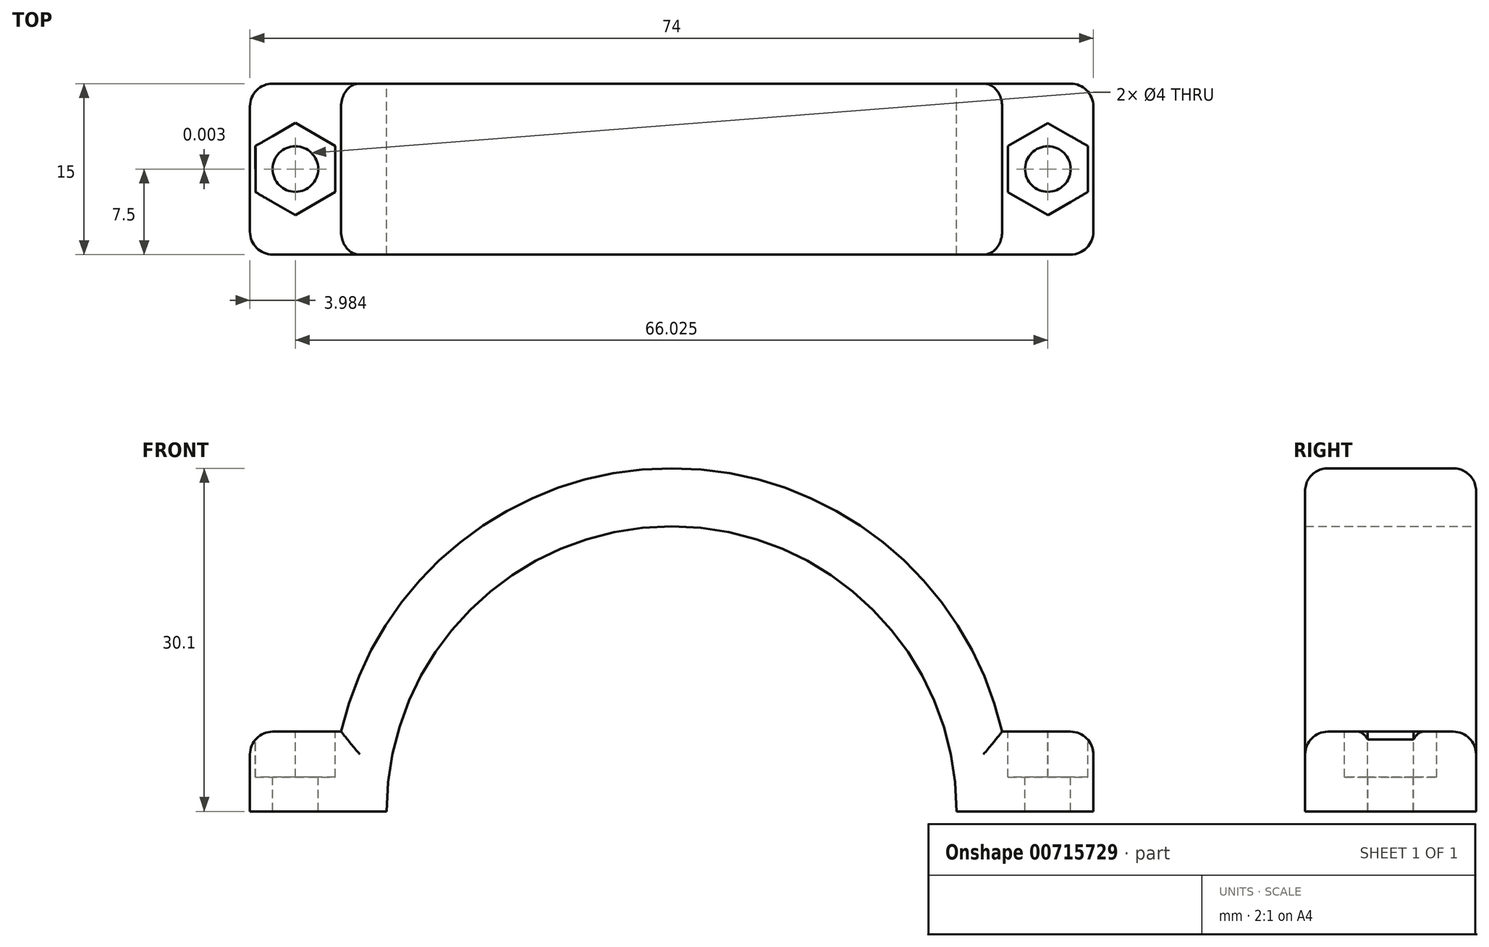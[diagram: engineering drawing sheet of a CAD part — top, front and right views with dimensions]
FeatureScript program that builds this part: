
annotation { "Feature Type Name" : "Feature", "Feature Type Description" : "" }
export const myFeature = defineFeature(function(context is Context, id is Id, definition is map)
    precondition{}
    {
        {
            var Q0;
            Q0=qCreatedBy(makeId("Front.planeOp"),FACE);
            var sketch = newSketch(context, id + "F0", { "sketchPlane" : qUnion([Q0])});
            skArc(sketch, "E0", {"start": v(26.87, 0.03) * mm, "mid": v(1.87, 25.02) * mm, "end": v(-23.13, 0.03) * mm});
            skLineSegment(sketch, "E1", {"start": v(26.87, 0.03) * mm, "end": v(38.87, 0.03) * mm});
            skLineSegment(sketch, "E2", {"start": v(38.87, 0.03) * mm, "end": v(38.87, 7.03) * mm});
            skLineSegment(sketch, "E3", {"start": v(38.87, 7.03) * mm, "end": v(30.87, 7.03) * mm});
            skLineSegment(sketch, "E4", {"start": v(-23.13, 0.03) * mm, "end": v(-35.13, 0.03) * mm});
            skLineSegment(sketch, "E5", {"start": v(-35.13, 0.03) * mm, "end": v(-35.13, 7.03) * mm});
            skLineSegment(sketch, "E6", {"start": v(-35.13, 7.03) * mm, "end": v(-27.13, 7.03) * mm});
            skArc(sketch, "E7", {"start": v(30.87, 7.03) * mm, "mid": v(1.87, 30.13) * mm, "end": v(-27.13, 7.03) * mm});
            skSolve(sketch);
        }
        {
            var Q0;
            Q0 = qSketchRegion(id + "F0", true);
            extrude(context, id + "F1", {"entities" : qUnion([Q0]), "depth" : 15 * mm, "offsetDistance" : 25 * mm});
        }
        {
            var Q0;
            Q0=makeQuery(id+"F1.opExtrude","CAP_EDGE",EDGE,{"disambiguationData":[OSD([sQuery(id+"F0.wireOp",EDGE,"E7")])],"isStart":false});
            var Q1;
            Q1=makeQuery(id+"F1.opExtrude","CAP_EDGE",EDGE,{"disambiguationData":[OSD([sQuery(id+"F0.wireOp",EDGE,"E3")])],"isStart":false});
            var Q2;
            Q2=makeQuery(id+"F1.opExtrude","CAP_EDGE",EDGE,{"disambiguationData":[OSD([sQuery(id+"F0.wireOp",EDGE,"E2")])],"isStart":false});
            var Q3;
            Q3=makeQuery(id+"F1.opExtrude","SWEPT_EDGE",EDGE,{"disambiguationData":[OSD([sQuery(id+"F0.wireOp",EDGE,"E2"),sQuery(id+"F0.wireOp",EDGE,"E3")])]});
            var Q4;
            Q4=makeQuery(id+"F1.opExtrude","CAP_EDGE",EDGE,{"disambiguationData":[OSD([sQuery(id+"F0.wireOp",EDGE,"E6")])],"isStart":false});
            var Q5;
            Q5=makeQuery(id+"F1.opExtrude","CAP_EDGE",EDGE,{"disambiguationData":[OSD([sQuery(id+"F0.wireOp",EDGE,"E5")])],"isStart":false});
            var Q6;
            Q6=makeQuery(id+"F1.opExtrude","SWEPT_EDGE",EDGE,{"disambiguationData":[OSD([sQuery(id+"F0.wireOp",EDGE,"E5"),sQuery(id+"F0.wireOp",EDGE,"E6")])]});
            var Q7;
            Q7=makeQuery(id+"F1.opExtrude","CAP_EDGE",EDGE,{"disambiguationData":[OSD([sQuery(id+"F0.wireOp",EDGE,"E7")])],"isStart":true});
            var Q8;
            Q8=makeQuery(id+"F1.opExtrude","CAP_EDGE",EDGE,{"disambiguationData":[OSD([sQuery(id+"F0.wireOp",EDGE,"E6")])],"isStart":true});
            var Q9;
            Q9=makeQuery(id+"F1.opExtrude","CAP_EDGE",EDGE,{"disambiguationData":[OSD([sQuery(id+"F0.wireOp",EDGE,"E5")])],"isStart":true});
            var Q10;
            Q10=makeQuery(id+"F1.opExtrude","CAP_EDGE",EDGE,{"disambiguationData":[OSD([sQuery(id+"F0.wireOp",EDGE,"E3")])],"isStart":true});
            var Q11;
            Q11=makeQuery(id+"F1.opExtrude","CAP_EDGE",EDGE,{"disambiguationData":[OSD([sQuery(id+"F0.wireOp",EDGE,"E2")])],"isStart":true});
            fillet(context, id + "F2", {"entities" : qUnion([Q0, Q1, Q2, Q3, Q4, Q5, Q6, Q7, Q8, Q9, Q10, Q11]), "radius" : 2 * mm, "tangentPropagation" : true, "allowEdgeOverflow" : false});
        }
        {
            var Q0;
            Q0=makeQuery(id+"F1.opExtrude","SWEPT_FACE",FACE,{"disambiguationData":[OSD([sQuery(id+"F0.wireOp",EDGE,"E3")])]});
            var sketch = newSketch(context, id + "F3", { "sketchPlane" : qUnion([Q0])});
            skCircle(sketch, "E8", {"center": v(34.88, -7.5) * mm, "radius": 2 * mm});
            skCircle(sketch, "E9.cCircle", {"center": v(34.88, -7.5) * mm, "radius": 3.5 * mm, "construction": true});
            skLineSegment(sketch, "E9.0", {"start": v(31.38, -5.49) * mm, "end": v(34.87, -3.46) * mm});
            skLineSegment(sketch, "E9.1", {"start": v(34.87, -3.46) * mm, "end": v(38.38, -5.47) * mm});
            skLineSegment(sketch, "E9.2", {"start": v(38.38, -5.47) * mm, "end": v(38.38, -9.51) * mm});
            skLineSegment(sketch, "E9.3", {"start": v(38.38, -9.51) * mm, "end": v(34.89, -11.54) * mm});
            skLineSegment(sketch, "E9.4", {"start": v(34.89, -11.54) * mm, "end": v(31.38, -9.53) * mm});
            skLineSegment(sketch, "E9.5", {"start": v(31.38, -9.53) * mm, "end": v(31.38, -5.49) * mm});
            skPoint(sketch, "E9.0.midPoint", {"position": v(33.12, -4.47) * mm});
            skSolve(sketch);
        }
        {
            var Q0;
            {var subQ0=sQuery(id+"F3.wireOp",EDGE,"E8");var subQ1=sQuery(id+"F0.wireOp",EDGE,"E3");var subQ2=makeQuery(id+"F2.opFillet","BLEND_EDGE",EDGE,{"blendedFrom":[makeQuery(id+"F1.opExtrude","SWEPT_EDGE",EDGE,{"disambiguationData":[OSD([sQuery(id+"F0.wireOp",EDGE,"E2"),subQ1])]}),makeQuery(id+"F1.opExtrude","SWEPT_FACE",FACE,{"disambiguationData":[OSD([subQ1])]})],"blendedInto":[makeQuery(id+"F1.opExtrude","SWEPT_FACE",FACE,{"disambiguationData":[OSD([subQ1])]})]});var subQ3=makeQuery(id+"F3.imprint","INTERSECT",VERTEX,{"disambiguationData":[OD(0.0)],"derivedFrom":[subQ2,subQ0]});Q0=makeQuery(id+"F3.imprint","IMPRINT",FACE,{"disambiguationData":[TD([[makeQuery(id+"F3.imprint","IMPRINT",EDGE,{"disambiguationData":[TD([[subQ3,-1.0]])],"derivedFrom":subQ0}),1.0]])]});}
            extrude(context, id + "F4", {"entities" : qUnion([Q0]), "operationType" : NewBodyOperationType.REMOVE, "oppositeDirection" : true, "depth" : 25 * mm, "offsetDistance" : 25 * mm});
        }
        {
            var Q0;
            {var subQ1=sQuery(id+"F3.wireOp",EDGE,"E9.0");Q0=makeQuery(id+"F3.imprint","IMPRINT",FACE,{"disambiguationData":[TD([[makeQuery(id+"F3.imprint","IMPRINT",EDGE,{"derivedFrom":subQ1}),-1.0]])]});}
            var Q1;
            {var subQ0=sQuery(id+"F3.wireOp",EDGE,"E9.2");Q1=makeQuery(id+"F3.imprint","IMPRINT",FACE,{"disambiguationData":[TD([[makeQuery(id+"F3.imprint","IMPRINT",EDGE,{"derivedFrom":subQ0}),-1.0]])]});}
            extrude(context, id + "F5", {"entities" : qUnion([Q0, Q1]), "operationType" : NewBodyOperationType.REMOVE, "oppositeDirection" : true, "depth" : 4 * mm, "offsetDistance" : 25 * mm});
        }
        {
            var Q0;
            {var subQ0=sQuery(id+"F3.wireOp",EDGE,"E8");var subQ1=sQuery(id+"F0.wireOp",EDGE,"E3");var subQ2=makeQuery(id+"F2.opFillet","BLEND_EDGE",EDGE,{"blendedFrom":[makeQuery(id+"F1.opExtrude","SWEPT_EDGE",EDGE,{"disambiguationData":[OSD([sQuery(id+"F0.wireOp",EDGE,"E2"),subQ1])]}),makeQuery(id+"F1.opExtrude","SWEPT_FACE",FACE,{"disambiguationData":[OSD([subQ1])]})],"blendedInto":[makeQuery(id+"F1.opExtrude","SWEPT_FACE",FACE,{"disambiguationData":[OSD([subQ1])]})]});var subQ3=makeQuery(id+"F3.imprint","INTERSECT",VERTEX,{"disambiguationData":[OD(0.0)],"derivedFrom":[subQ2,subQ0]});Q0=makeQuery(id+"F3.imprint","IMPRINT",FACE,{"disambiguationData":[TD([[makeQuery(id+"F3.imprint","IMPRINT",EDGE,{"disambiguationData":[TD([[subQ3,1.0]])],"derivedFrom":subQ0}),1.0]])]});}
            extrude(context, id + "F6", {"entities" : qUnion([Q0]), "operationType" : NewBodyOperationType.REMOVE, "oppositeDirection" : true, "depth" : 25 * mm, "offsetDistance" : 25 * mm});
        }
        {
            var Q0;
            Q0=makeQuery(id+"F1.opExtrude","SWEPT_FACE",FACE,{"disambiguationData":[OSD([sQuery(id+"F0.wireOp",EDGE,"E6")])]});
            var sketch = newSketch(context, id + "F7", { "sketchPlane" : qUnion([Q0])});
            skCircle(sketch, "E10", {"center": v(-31.15, -7.5) * mm, "radius": 2 * mm});
            skCircle(sketch, "E11.cCircle", {"center": v(-31.15, -7.5) * mm, "radius": 3.5 * mm, "construction": true});
            skLineSegment(sketch, "E11.0", {"start": v(-34.65, -5.48) * mm, "end": v(-31.15, -3.46) * mm});
            skLineSegment(sketch, "E11.1", {"start": v(-31.15, -3.46) * mm, "end": v(-27.65, -5.47) * mm});
            skLineSegment(sketch, "E11.2", {"start": v(-27.65, -5.47) * mm, "end": v(-27.64, -9.51) * mm});
            skLineSegment(sketch, "E11.3", {"start": v(-27.64, -9.51) * mm, "end": v(-31.14, -11.54) * mm});
            skLineSegment(sketch, "E11.4", {"start": v(-31.14, -11.54) * mm, "end": v(-34.64, -9.52) * mm});
            skLineSegment(sketch, "E11.5", {"start": v(-34.64, -9.52) * mm, "end": v(-34.65, -5.48) * mm});
            skPoint(sketch, "E11.0.midPoint", {"position": v(-32.9, -4.47) * mm});
            skSolve(sketch);
        }
        {
            var Q0;
            {var subQ0=sQuery(id+"F7.wireOp",EDGE,"E10");var subQ1=sQuery(id+"F0.wireOp",EDGE,"E6");var subQ2=makeQuery(id+"F2.opFillet","BLEND_EDGE",EDGE,{"blendedFrom":[makeQuery(id+"F1.opExtrude","SWEPT_EDGE",EDGE,{"disambiguationData":[OSD([sQuery(id+"F0.wireOp",EDGE,"E5"),subQ1])]}),makeQuery(id+"F1.opExtrude","SWEPT_FACE",FACE,{"disambiguationData":[OSD([subQ1])]})],"blendedInto":[makeQuery(id+"F1.opExtrude","SWEPT_FACE",FACE,{"disambiguationData":[OSD([subQ1])]})]});var subQ3=makeQuery(id+"F7.imprint","INTERSECT",VERTEX,{"disambiguationData":[OD(0.0)],"derivedFrom":[subQ2,subQ0]});Q0=makeQuery(id+"F7.imprint","IMPRINT",FACE,{"disambiguationData":[TD([[makeQuery(id+"F7.imprint","IMPRINT",EDGE,{"disambiguationData":[TD([[subQ3,1.0]])],"derivedFrom":subQ0}),1.0]])]});}
            extrude(context, id + "F8", {"entities" : qUnion([Q0]), "operationType" : NewBodyOperationType.REMOVE, "oppositeDirection" : true, "depth" : 25 * mm, "offsetDistance" : 25 * mm});
        }
        {
            var Q0;
            {var subQ0=sQuery(id+"F7.wireOp",EDGE,"E11.5");Q0=makeQuery(id+"F7.imprint","IMPRINT",FACE,{"disambiguationData":[TD([[makeQuery(id+"F7.imprint","IMPRINT",EDGE,{"derivedFrom":subQ0}),-1.0]])]});}
            var Q1;
            {var subQ6=sQuery(id+"F7.wireOp",EDGE,"E11.1");Q1=makeQuery(id+"F7.imprint","IMPRINT",FACE,{"disambiguationData":[TD([[makeQuery(id+"F7.imprint","IMPRINT",EDGE,{"derivedFrom":subQ6}),-1.0]])]});}
            extrude(context, id + "F9", {"entities" : qUnion([Q0, Q1]), "operationType" : NewBodyOperationType.REMOVE, "oppositeDirection" : true, "depth" : 4 * mm, "offsetDistance" : 25 * mm});
        }
        {
            var Q0;
            {var subQ0=sQuery(id+"F7.wireOp",EDGE,"E10");var subQ1=sQuery(id+"F0.wireOp",EDGE,"E6");var subQ2=makeQuery(id+"F2.opFillet","BLEND_EDGE",EDGE,{"blendedFrom":[makeQuery(id+"F1.opExtrude","SWEPT_EDGE",EDGE,{"disambiguationData":[OSD([sQuery(id+"F0.wireOp",EDGE,"E5"),subQ1])]}),makeQuery(id+"F1.opExtrude","SWEPT_FACE",FACE,{"disambiguationData":[OSD([subQ1])]})],"blendedInto":[makeQuery(id+"F1.opExtrude","SWEPT_FACE",FACE,{"disambiguationData":[OSD([subQ1])]})]});var subQ3=makeQuery(id+"F7.imprint","INTERSECT",VERTEX,{"disambiguationData":[OD(0.0)],"derivedFrom":[subQ2,subQ0]});Q0=makeQuery(id+"F7.imprint","IMPRINT",FACE,{"disambiguationData":[TD([[makeQuery(id+"F7.imprint","IMPRINT",EDGE,{"disambiguationData":[TD([[subQ3,-1.0]])],"derivedFrom":subQ0}),1.0]])]});}
            extrude(context, id + "F10", {"entities" : qUnion([Q0]), "operationType" : NewBodyOperationType.REMOVE, "oppositeDirection" : true, "depth" : 25 * mm, "offsetDistance" : 25 * mm});
        }
    });
